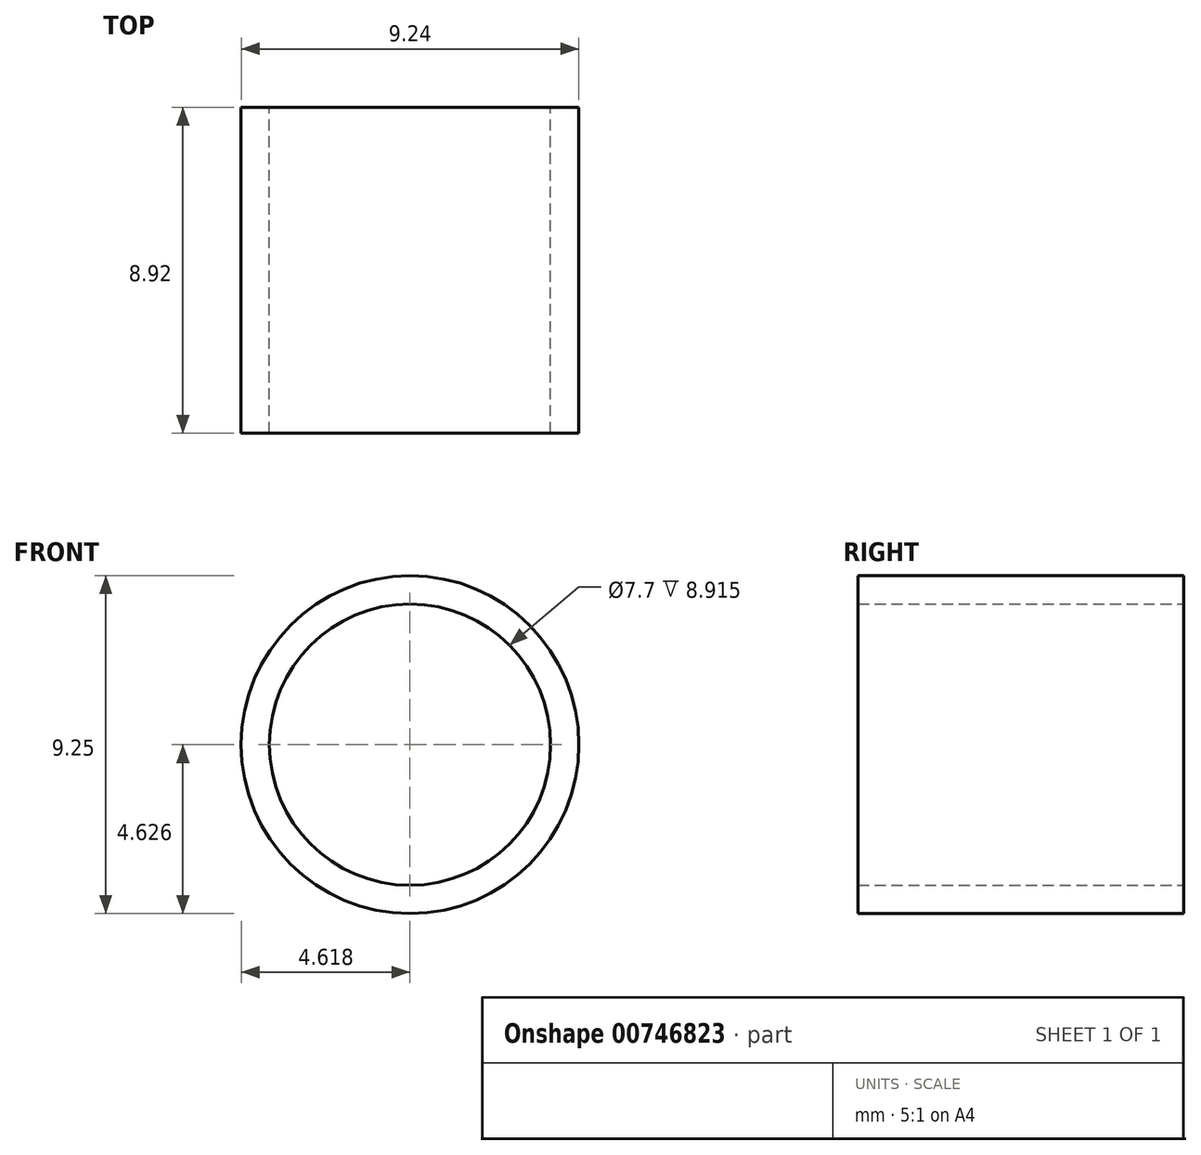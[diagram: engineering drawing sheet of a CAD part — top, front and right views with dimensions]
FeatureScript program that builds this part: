
annotation { "Feature Type Name" : "Feature", "Feature Type Description" : "" }
export const myFeature = defineFeature(function(context is Context, id is Id, definition is map)
    precondition{}
    {
        {
            var Q0;
            Q0=qCreatedBy(makeId("Front.planeOp"),FACE);
            var sketch = newSketch(context, id + "F0", { "sketchPlane" : qUnion([Q0])});
            skCircle(sketch, "E0", {"center": v(-35.58, 25.42) * mm, "radius": 4.62 * mm});
            skCircle(sketch, "E1", {"center": v(-35.58, 25.42) * mm, "radius": 3.85 * mm});
            skSolve(sketch);
        }
        {
            var Q0;
            Q0=qCreatedBy(makeId("Front.planeOp"),FACE);
            cPlane(context, id + "F1", {"entities" : qUnion([Q0]), "cplaneType" : CPlaneType.OFFSET, "offset" : 9.14 * mm, "width" : 152.4 * mm, "height" : 152.4 * mm});
        }
        {
            var Q0;
            Q0=makeQuery(id+"F0.imprint","IMPRINT",FACE,{"disambiguationData":[TD([[makeQuery(id+"F0.imprint","IMPRINT",EDGE,{"derivedFrom":sQuery(id+"F0.wireOp",EDGE,"E0")}),1.0]])]});
            extrude(context, id + "F2", {"entities" : qUnion([Q0]), "depth" : 8.92 * mm, "offsetDistance" : 25.4 * mm});
        }
    });
